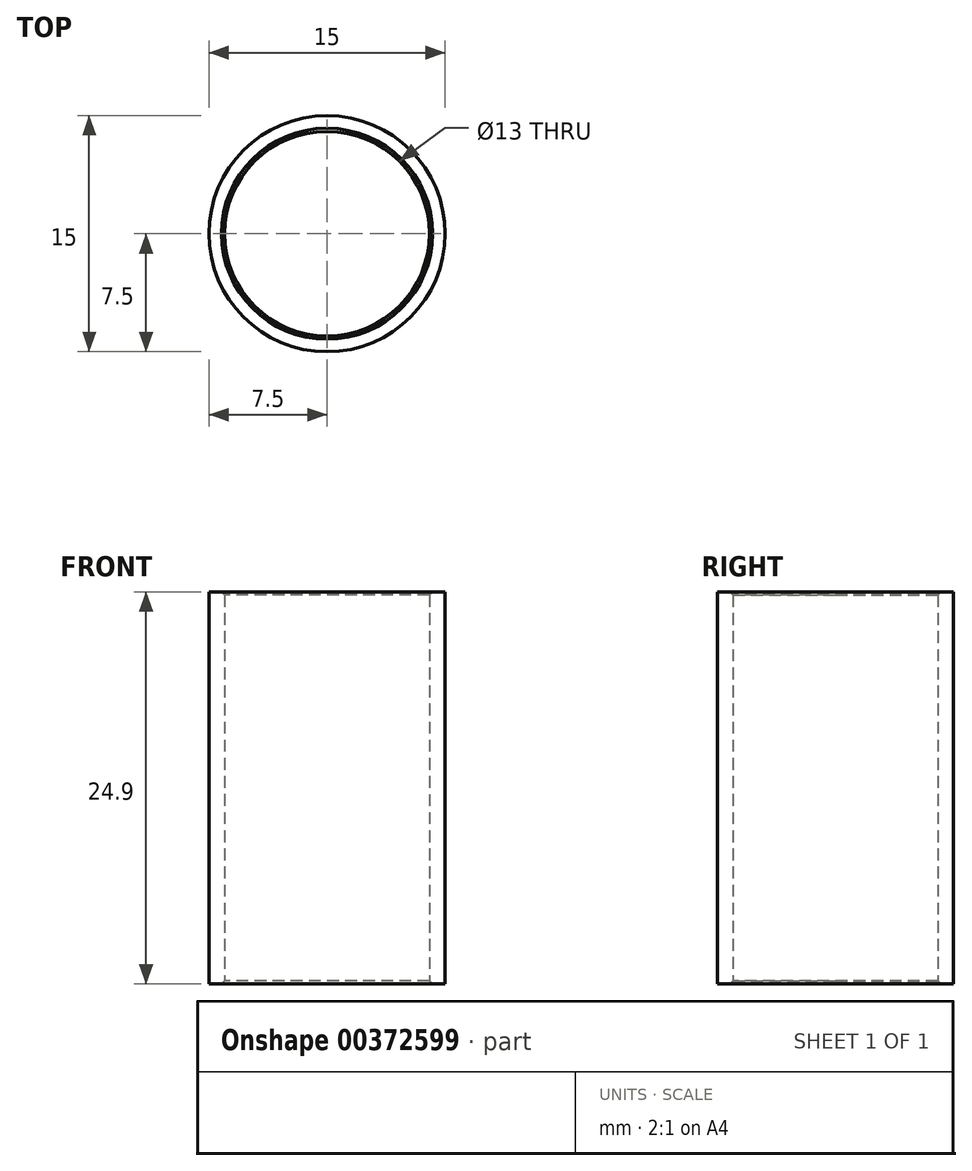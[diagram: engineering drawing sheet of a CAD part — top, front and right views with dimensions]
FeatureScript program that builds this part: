
annotation { "Feature Type Name" : "Feature", "Feature Type Description" : "" }
export const myFeature = defineFeature(function(context is Context, id is Id, definition is map)
    precondition{}
    {
        {
            var Q0;
            Q0=qCreatedBy(makeId("Top.planeOp"),FACE);
            var sketch = newSketch(context, id + "F0", { "sketchPlane" : qUnion([Q0])});
            skCircle(sketch, "E0", {"center": v(0, 0) * mm, "radius": 6.5 * mm});
            skCircle(sketch, "E1", {"center": v(0, 0) * mm, "radius": 7.5 * mm});
            skSolve(sketch);
        }
        {
            var Q0;
            Q0=makeQuery(id+"F0.imprint","IMPRINT",FACE,{"disambiguationData":[TD([[makeQuery(id+"F0.imprint","IMPRINT",EDGE,{"derivedFrom":sQuery(id+"F0.wireOp",EDGE,"E0")}),-1.0]])]});
            extrude(context, id + "F1", {"entities" : qUnion([Q0]), "depth" : 24.9 * mm});
        }
        {
            var Q0;
            Q0=makeQuery(id+"F1.opExtrude","CAP_EDGE",EDGE,{"disambiguationData":[OSD([sQuery(id+"F0.wireOp",EDGE,"E0")])],"isStart":true});
            var Q1;
            Q1=makeQuery(id+"F1.opExtrude","CAP_EDGE",EDGE,{"disambiguationData":[OSD([sQuery(id+"F0.wireOp",EDGE,"E0")])],"isStart":false});
            chamfer(context, id + "F2", {"entities" : qUnion([Q0, Q1]), "width" : 0.2 * mm, "tangentPropagation" : true});
        }
    });
